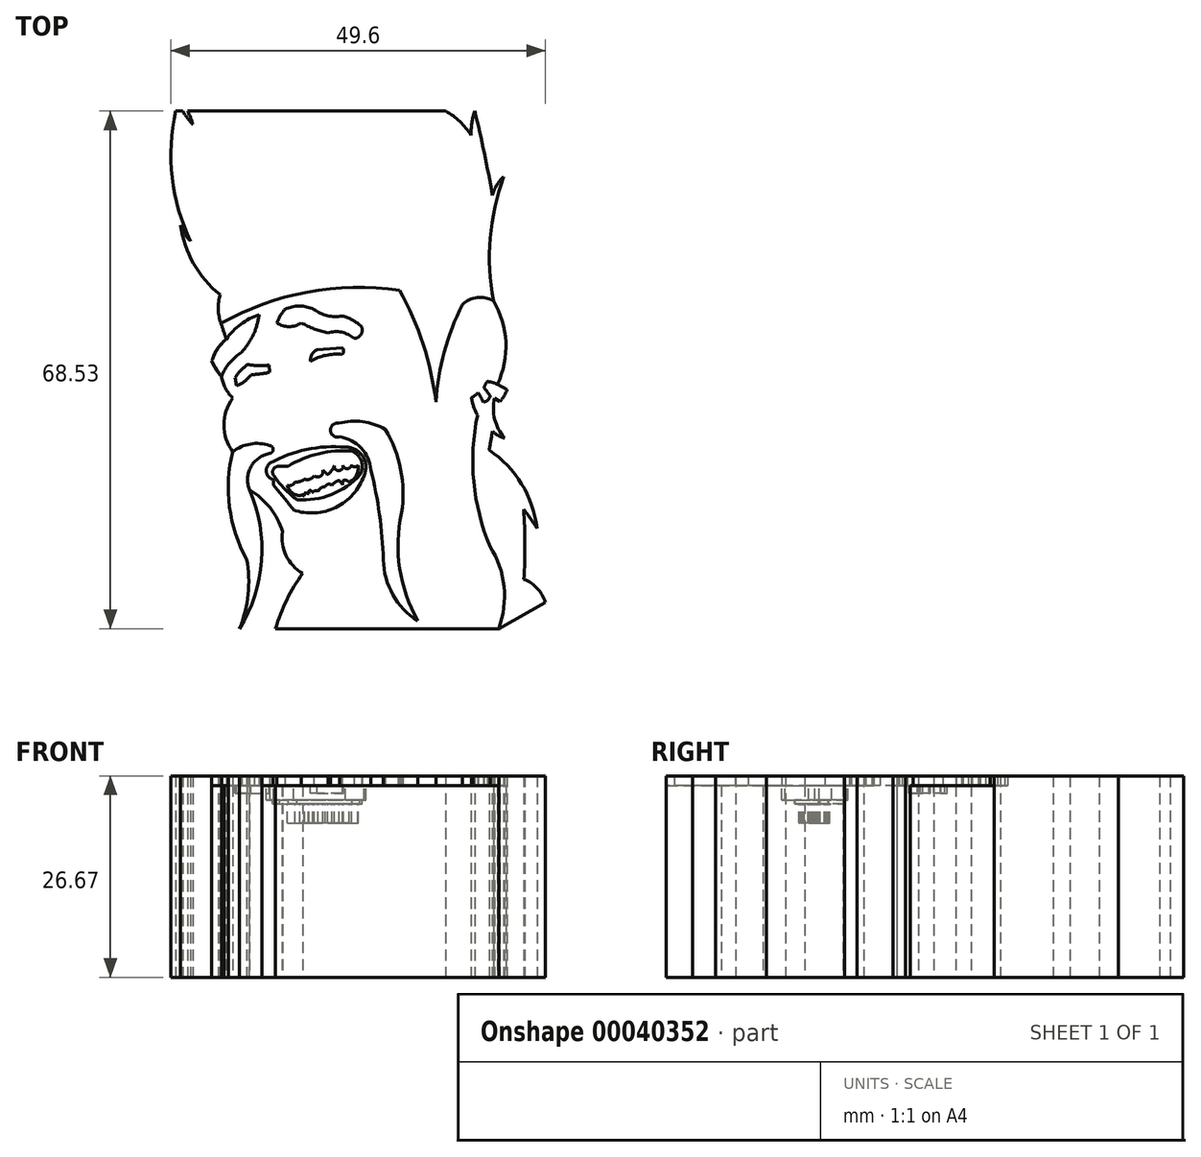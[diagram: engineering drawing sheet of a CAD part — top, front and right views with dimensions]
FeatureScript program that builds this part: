
annotation { "Feature Type Name" : "Feature", "Feature Type Description" : "" }
export const myFeature = defineFeature(function(context is Context, id is Id, definition is map)
    precondition{}
    {
        {
            var Q0;
            Q0=qCreatedBy(makeId("Top.planeOp"),FACE);
            var sketch = newSketch(context, id + "F0", { "sketchPlane" : qUnion([Q0])});
            skPoint(sketch, "E0", {"position": v(10.3, 53.46) * mm});
            skPoint(sketch, "E1", {"position": v(49.25, 68.53) * mm});
            skPoint(sketch, "E2", {"position": v(53.1, 59.84) * mm});
            skPoint(sketch, "E3", {"position": v(51.73, 43.41) * mm});
            skPoint(sketch, "E4", {"position": v(15.54, 44.24) * mm});
            skPoint(sketch, "E5", {"position": v(51.6, 57.35) * mm});
            skPoint(sketch, "E6", {"position": v(52.26, 32.34) * mm});
            skPoint(sketch, "E7", {"position": v(51.24, 31) * mm});
            skPoint(sketch, "E8", {"position": v(50.35, 29.98) * mm});
            skPoint(sketch, "E9", {"position": v(49.07, 29.21) * mm});
            skPoint(sketch, "E10", {"position": v(47.66, 29.02) * mm});
            skPoint(sketch, "E11", {"position": v(49.7, 28.13) * mm});
            skPoint(sketch, "E12", {"position": v(50.86, 28.7) * mm});
            skPoint(sketch, "E13", {"position": v(52.58, 30.04) * mm});
            skPoint(sketch, "E14", {"position": v(53.57, 31.65) * mm});
            skArc(sketch, "E15", {"start": v(52.26, 32.34) * mm, "mid": v(53.39, 37.94) * mm, "end": v(51.73, 43.41) * mm});
            skArc(sketch, "E16", {"start": v(52.58, 30.04) * mm, "mid": v(53.15, 30.8) * mm, "end": v(53.57, 31.65) * mm});
            skLineSegment(sketch, "E17", {"start": v(51.24, 31) * mm, "end": v(52.58, 30.04) * mm});
            skLineSegment(sketch, "E18", {"start": v(53.57, 31.65) * mm, "end": v(52.26, 32.34) * mm});
            skPoint(sketch, "E19", {"position": v(45.4, 68.53) * mm});
            skPoint(sketch, "E20", {"position": v(11.23, 68.53) * mm});
            skPoint(sketch, "E21", {"position": v(10.6, 68.53) * mm});
            skPoint(sketch, "E22", {"position": v(9.67, 68.53) * mm});
            skPoint(sketch, "E23", {"position": v(48.8, 65.33) * mm});
            skPoint(sketch, "E24", {"position": v(11.66, 51.27) * mm});
            skPoint(sketch, "E25", {"position": v(11.94, 66.75) * mm});
            skArc(sketch, "E26", {"start": v(10.6, 68.53) * mm, "mid": v(11.22, 67.6) * mm, "end": v(11.94, 66.75) * mm});
            skArc(sketch, "E27", {"start": v(11.94, 66.75) * mm, "mid": v(11.64, 67.66) * mm, "end": v(11.23, 68.53) * mm});
            skArc(sketch, "E28", {"start": v(48.8, 65.33) * mm, "mid": v(47.3, 67.15) * mm, "end": v(45.4, 68.53) * mm});
            skArc(sketch, "E29", {"start": v(49.25, 68.53) * mm, "mid": v(48.88, 66.95) * mm, "end": v(48.8, 65.33) * mm});
            skArc(sketch, "E30", {"start": v(51.6, 57.35) * mm, "mid": v(50.54, 62.97) * mm, "end": v(49.25, 68.53) * mm});
            skArc(sketch, "E31", {"start": v(53.1, 59.84) * mm, "mid": v(52.17, 58.7) * mm, "end": v(51.6, 57.35) * mm});
            skArc(sketch, "E32", {"start": v(53.1, 59.84) * mm, "mid": v(51.32, 51.72) * mm, "end": v(51.73, 43.41) * mm});
            skArc(sketch, "E33", {"start": v(9.67, 68.53) * mm, "mid": v(9.2, 59.73) * mm, "end": v(11.66, 51.27) * mm});
            skArc(sketch, "E34", {"start": v(10.3, 53.46) * mm, "mid": v(10.85, 52.28) * mm, "end": v(11.66, 51.27) * mm});
            skArc(sketch, "E35", {"start": v(10.3, 53.46) * mm, "mid": v(12.03, 48.34) * mm, "end": v(15.54, 44.24) * mm});
            skLineSegment(sketch, "E36", {"start": v(9.67, 68.53) * mm, "end": v(10.6, 68.53) * mm});
            skLineSegment(sketch, "E37", {"start": v(45.4, 68.53) * mm, "end": v(11.23, 68.53) * mm});
            skPoint(sketch, "E38", {"position": v(15.66, 40.4) * mm});
            skPoint(sketch, "E39", {"position": v(16.37, 38.34) * mm});
            skPoint(sketch, "E40", {"position": v(14.46, 35.44) * mm});
            skPoint(sketch, "E41", {"position": v(15.73, 33.39) * mm});
            skArc(sketch, "E42", {"start": v(15.54, 44.24) * mm, "mid": v(15.3, 42.3) * mm, "end": v(15.66, 40.4) * mm});
            skArc(sketch, "E43", {"start": v(16.37, 38.34) * mm, "mid": v(16.02, 39.37) * mm, "end": v(15.66, 40.4) * mm});
            skArc(sketch, "E44", {"start": v(16.37, 38.34) * mm, "mid": v(15.19, 37.04) * mm, "end": v(14.46, 35.44) * mm});
            skArc(sketch, "E45", {"start": v(14.46, 35.44) * mm, "mid": v(15, 34.35) * mm, "end": v(15.73, 33.39) * mm});
            skPoint(sketch, "E46", {"position": v(48.02, 25.2) * mm});
            skPoint(sketch, "E47", {"position": v(17.2, 30.53) * mm});
            skArc(sketch, "E48", {"start": v(15.73, 33.39) * mm, "mid": v(16.25, 31.84) * mm, "end": v(17.2, 30.53) * mm});
            skArc(sketch, "E49", {"start": v(17.2, 30.53) * mm, "mid": v(16.05, 26.97) * mm, "end": v(17.2, 23.4) * mm});
            skPoint(sketch, "E50", {"position": v(51.9, 30.52) * mm});
            skPoint(sketch, "E51", {"position": v(53.2, 25.24) * mm});
            skPoint(sketch, "E52", {"position": v(51.61, 26.15) * mm});
            skPoint(sketch, "E53", {"position": v(51.17, 23.63) * mm});
            skPoint(sketch, "E54", {"position": v(57.51, 13.28) * mm});
            skPoint(sketch, "E55", {"position": v(55.74, 15.8) * mm});
            skArc(sketch, "E56", {"start": v(51.9, 30.52) * mm, "mid": v(51.9, 27.72) * mm, "end": v(53.2, 25.24) * mm});
            skArc(sketch, "E57", {"start": v(51.61, 26.15) * mm, "mid": v(52.34, 25.59) * mm, "end": v(53.2, 25.24) * mm});
            skArc(sketch, "E58", {"start": v(51.17, 23.63) * mm, "mid": v(51.4, 24.89) * mm, "end": v(51.61, 26.15) * mm});
            skArc(sketch, "E59", {"start": v(57.51, 13.28) * mm, "mid": v(55.47, 19.15) * mm, "end": v(51.17, 23.63) * mm});
            skArc(sketch, "E60", {"start": v(57.51, 13.28) * mm, "mid": v(56.66, 14.56) * mm, "end": v(55.74, 15.8) * mm});
            skPoint(sketch, "E61", {"position": v(55.8, 6.52) * mm});
            skPoint(sketch, "E62", {"position": v(58.63, 3.47) * mm});
            skPoint(sketch, "E63", {"position": v(52.44, 0) * mm});
            skPoint(sketch, "E64", {"position": v(18.11, 0) * mm});
            skPoint(sketch, "E65", {"position": v(22.88, 0) * mm});
            skArc(sketch, "E66", {"start": v(55.8, 6.52) * mm, "mid": v(55.9, 11.16) * mm, "end": v(55.74, 15.8) * mm});
            skArc(sketch, "E67", {"start": v(58.63, 3.47) * mm, "mid": v(57.56, 5.32) * mm, "end": v(55.8, 6.52) * mm});
            skLineSegment(sketch, "E68", {"start": v(58.63, 3.47) * mm, "end": v(52.44, 0) * mm});
            skLineSegment(sketch, "E69", {"start": v(22.88, 0) * mm, "end": v(52.44, 0) * mm});
            skPoint(sketch, "E70", {"position": v(26.46, 7.3) * mm});
            skPoint(sketch, "E71", {"position": v(23.83, 12.83) * mm});
            skPoint(sketch, "E72", {"position": v(19.43, 18.36) * mm});
            skArc(sketch, "E73", {"start": v(18.11, 0) * mm, "mid": v(21.05, 9.01) * mm, "end": v(19.43, 18.36) * mm});
            skArc(sketch, "E74", {"start": v(23.83, 12.83) * mm, "mid": v(22.15, 16) * mm, "end": v(19.43, 18.36) * mm});
            skArc(sketch, "E75", {"start": v(23.83, 12.83) * mm, "mid": v(24.3, 9.66) * mm, "end": v(26.46, 7.3) * mm});
            skArc(sketch, "E76", {"start": v(26.46, 7.3) * mm, "mid": v(24.37, 3.8) * mm, "end": v(22.88, 0) * mm});
            skArc(sketch, "E77", {"start": v(17.2, 23.4) * mm, "mid": v(16.8, 16.12) * mm, "end": v(19.05, 9.19) * mm});
            skArc(sketch, "E78", {"start": v(18.11, 0) * mm, "mid": v(19.26, 4.52) * mm, "end": v(19.05, 9.19) * mm});
            skSolve(sketch);
        }
        {
            var Q0;
            Q0 = qSketchRegion(id + "F0", true);
            extrude(context, id + "F1", {"entities" : qUnion([Q0]), "depth" : 25.4 * mm});
        }
        {
            var Q0;
            Q0=makeQuery(id+"F1.opExtrude","CAP_FACE",FACE,{"disambiguationData":[OSD([sQuery(id+"F0.wireOp",EDGE,"E15"),sQuery(id+"F0.wireOp",EDGE,"E16"),sQuery(id+"F0.wireOp",EDGE,"E17"),sQuery(id+"F0.wireOp",EDGE,"E18"),sQuery(id+"F0.wireOp",EDGE,"E26"),sQuery(id+"F0.wireOp",EDGE,"E27"),sQuery(id+"F0.wireOp",EDGE,"E28"),sQuery(id+"F0.wireOp",EDGE,"E29"),sQuery(id+"F0.wireOp",EDGE,"E30"),sQuery(id+"F0.wireOp",EDGE,"E31"),sQuery(id+"F0.wireOp",EDGE,"E32"),sQuery(id+"F0.wireOp",EDGE,"E33"),sQuery(id+"F0.wireOp",EDGE,"E34"),sQuery(id+"F0.wireOp",EDGE,"E35"),sQuery(id+"F0.wireOp",EDGE,"E36"),sQuery(id+"F0.wireOp",EDGE,"E37"),sQuery(id+"F0.wireOp",EDGE,"E42"),sQuery(id+"F0.wireOp",EDGE,"E43"),sQuery(id+"F0.wireOp",EDGE,"E44"),sQuery(id+"F0.wireOp",EDGE,"E45"),sQuery(id+"F0.wireOp",EDGE,"E48"),sQuery(id+"F0.wireOp",EDGE,"E49"),sQuery(id+"F0.wireOp",EDGE,"E56"),sQuery(id+"F0.wireOp",EDGE,"E57"),sQuery(id+"F0.wireOp",EDGE,"E58"),sQuery(id+"F0.wireOp",EDGE,"E59"),sQuery(id+"F0.wireOp",EDGE,"E60"),sQuery(id+"F0.wireOp",EDGE,"E66"),sQuery(id+"F0.wireOp",EDGE,"E67"),sQuery(id+"F0.wireOp",EDGE,"E68"),sQuery(id+"F0.wireOp",EDGE,"E69"),sQuery(id+"F0.wireOp",EDGE,"E73"),sQuery(id+"F0.wireOp",EDGE,"E74"),sQuery(id+"F0.wireOp",EDGE,"E75"),sQuery(id+"F0.wireOp",EDGE,"E76"),sQuery(id+"F0.wireOp",EDGE,"E77"),sQuery(id+"F0.wireOp",EDGE,"E78")])],"isStart":false});
            var sketch = newSketch(context, id + "F2", { "sketchPlane" : qUnion([Q0])});
            skArc(sketch, "E79", {"start": v(39.3, 44.83) * mm, "mid": v(27.11, 44.57) * mm, "end": v(15.66, 40.4) * mm});
            skArc(sketch, "E80", {"start": v(44.11, 30.03) * mm, "mid": v(42.44, 37.67) * mm, "end": v(39.3, 44.83) * mm});
            skArc(sketch, "E81", {"start": v(47.62, 42.9) * mm, "mid": v(45.24, 36.64) * mm, "end": v(44.11, 30.03) * mm});
            skArc(sketch, "E82", {"start": v(51.73, 43.41) * mm, "mid": v(49.59, 43.85) * mm, "end": v(47.62, 42.9) * mm});
            skArc(sketch, "E83", {"start": v(52.26, 32.34) * mm, "mid": v(53.4, 37.94) * mm, "end": v(51.73, 43.41) * mm});
            skArc(sketch, "E84", {"start": v(16.37, 38.34) * mm, "mid": v(16.1, 39.4) * mm, "end": v(15.66, 40.4) * mm});
            skArc(sketch, "E85", {"start": v(15.73, 33.39) * mm, "mid": v(16.11, 31.77) * mm, "end": v(17.2, 30.53) * mm});
            skArc(sketch, "E86", {"start": v(17.2, 30.53) * mm, "mid": v(16.1, 26.97) * mm, "end": v(17.2, 23.4) * mm});
            skArc(sketch, "E87", {"start": v(22.13, 24.25) * mm, "mid": v(19.57, 24.44) * mm, "end": v(17.2, 23.4) * mm});
            skArc(sketch, "E88", {"start": v(22.13, 23.2) * mm, "mid": v(22.57, 23.73) * mm, "end": v(22.13, 24.25) * mm});
            skArc(sketch, "E89", {"start": v(22.13, 23.2) * mm, "mid": v(19.63, 21.42) * mm, "end": v(19.43, 18.36) * mm});
            skArc(sketch, "E90", {"start": v(23.83, 12.83) * mm, "mid": v(22.08, 15.96) * mm, "end": v(19.43, 18.36) * mm});
            skArc(sketch, "E91", {"start": v(23.83, 12.83) * mm, "mid": v(24.12, 9.58) * mm, "end": v(26.46, 7.3) * mm});
            skArc(sketch, "E92", {"start": v(52.44, 0) * mm, "mid": v(53.15, 5.56) * mm, "end": v(51.3, 10.85) * mm});
            skArc(sketch, "E93", {"start": v(49.63, 28.28) * mm, "mid": v(49.14, 19.44) * mm, "end": v(51.3, 10.85) * mm});
            skArc(sketch, "E94", {"start": v(26.46, 7.3) * mm, "mid": v(27.3, 4.4) * mm, "end": v(29.14, 2) * mm});
            skArc(sketch, "E95", {"start": v(29.14, 2) * mm, "mid": v(40.75, 0.5) * mm, "end": v(52.44, 0) * mm});
            skArc(sketch, "E96", {"start": v(52.26, 32.34) * mm, "mid": v(51.62, 32.6) * mm, "end": v(50.94, 32.71) * mm});
            skArc(sketch, "E97", {"start": v(50.94, 32.71) * mm, "mid": v(50.67, 32.33) * mm, "end": v(50.48, 31.91) * mm});
            skArc(sketch, "E98", {"start": v(51.31, 30.82) * mm, "mid": v(50.9, 31.38) * mm, "end": v(50.48, 31.91) * mm});
            skArc(sketch, "E99", {"start": v(50.4, 29.97) * mm, "mid": v(50.99, 30.26) * mm, "end": v(51.31, 30.82) * mm});
            skArc(sketch, "E100", {"start": v(50.4, 29.97) * mm, "mid": v(50.1, 30.61) * mm, "end": v(49.71, 31.22) * mm});
            skArc(sketch, "E101", {"start": v(48.83, 30.6) * mm, "mid": v(49.3, 30.87) * mm, "end": v(49.71, 31.22) * mm});
            skArc(sketch, "E102", {"start": v(48.83, 30.6) * mm, "mid": v(49.12, 29.4) * mm, "end": v(49.63, 28.28) * mm});
            skArc(sketch, "E103", {"start": v(31.28, 27.2) * mm, "mid": v(30.17, 26.23) * mm, "end": v(31.39, 25.4) * mm});
            skArc(sketch, "E104", {"start": v(37.42, 26.41) * mm, "mid": v(34.43, 27.4) * mm, "end": v(31.28, 27.2) * mm});
            skArc(sketch, "E105", {"start": v(35.52, 21) * mm, "mid": v(34.21, 23.92) * mm, "end": v(31.39, 25.4) * mm});
            skArc(sketch, "E106", {"start": v(39.57, 15.3) * mm, "mid": v(39.46, 21.04) * mm, "end": v(37.42, 26.41) * mm});
            skArc(sketch, "E107", {"start": v(39.57, 15.3) * mm, "mid": v(39.32, 7.97) * mm, "end": v(41.72, 1.04) * mm});
            skArc(sketch, "E108", {"start": v(37.17, 9.1) * mm, "mid": v(38.43, 4.5) * mm, "end": v(41.72, 1.04) * mm});
            skArc(sketch, "E109", {"start": v(37.17, 9.1) * mm, "mid": v(36.66, 15.1) * mm, "end": v(35.52, 21) * mm});
            skArc(sketch, "E110", {"start": v(24.1, 42.28) * mm, "mid": v(23.53, 41.42) * mm, "end": v(23.08, 40.48) * mm});
            skArc(sketch, "E111", {"start": v(27.97, 42.28) * mm, "mid": v(26.04, 42.7) * mm, "end": v(24.1, 42.28) * mm});
            skArc(sketch, "E112", {"start": v(27.97, 42.28) * mm, "mid": v(29.75, 41.45) * mm, "end": v(31.7, 41.38) * mm});
            skArc(sketch, "E113", {"start": v(34.28, 39.97) * mm, "mid": v(33.1, 40.86) * mm, "end": v(31.7, 41.38) * mm});
            skArc(sketch, "E114", {"start": v(33.25, 38.42) * mm, "mid": v(34.17, 38.92) * mm, "end": v(34.28, 39.97) * mm});
            skArc(sketch, "E115", {"start": v(33.25, 38.42) * mm, "mid": v(31.64, 39.26) * mm, "end": v(29.84, 39.13) * mm});
            skArc(sketch, "E116", {"start": v(23.08, 40.48) * mm, "mid": v(24.69, 40) * mm, "end": v(26.3, 40.48) * mm});
            skArc(sketch, "E117", {"start": v(26.3, 40.48) * mm, "mid": v(28.02, 39.68) * mm, "end": v(29.84, 39.13) * mm});
            skPoint(sketch, "E118", {"position": v(20.7, 41.58) * mm});
            skPoint(sketch, "E119", {"position": v(18.45, 36.62) * mm});
            skArc(sketch, "E120", {"start": v(20.7, 41.58) * mm, "mid": v(18.28, 40.3) * mm, "end": v(16.37, 38.34) * mm});
            skArc(sketch, "E121", {"start": v(18.45, 36.62) * mm, "mid": v(16.83, 35.22) * mm, "end": v(15.73, 33.39) * mm});
            skArc(sketch, "E122", {"start": v(16.37, 38.34) * mm, "mid": v(15.21, 37.02) * mm, "end": v(14.46, 35.44) * mm});
            skArc(sketch, "E123", {"start": v(14.46, 35.44) * mm, "mid": v(15.05, 34.39) * mm, "end": v(15.73, 33.39) * mm});
            skArc(sketch, "E124", {"start": v(20.06, 39.13) * mm, "mid": v(20.46, 40.33) * mm, "end": v(20.7, 41.58) * mm});
            skArc(sketch, "E125", {"start": v(18.45, 36.62) * mm, "mid": v(19.32, 37.83) * mm, "end": v(20.06, 39.13) * mm});
            skSolve(sketch);
        }
        {
            var Q0;
            Q0=makeQuery(id+"F2.imprint","IMPRINT",FACE,{"disambiguationData":[TD([[makeQuery(id+"F2.imprint","IMPRINT",EDGE,{"derivedFrom":sQuery(id+"F2.wireOp",EDGE,"E79")}),-1.0]])]});
            var Q1;
            Q1=makeQuery(id+"F2.imprint","IMPRINT",FACE,{"disambiguationData":[TD([[makeQuery(id+"F2.imprint","IMPRINT",EDGE,{"derivedFrom":sQuery(id+"F2.wireOp",EDGE,"E92")}),-1.0]])]});
            var Q2;
            Q2=makeQuery(id+"F2.imprint","IMPRINT",FACE,{"disambiguationData":[TD([[makeQuery(id+"F2.imprint","IMPRINT",EDGE,{"derivedFrom":sQuery(id+"F2.wireOp",EDGE,"E87")}),1.0]])]});
            var Q3;
            Q3=makeQuery(id+"F2.imprint","IMPRINT",FACE,{"disambiguationData":[TD([[makeQuery(id+"F2.imprint","IMPRINT",EDGE,{"derivedFrom":sQuery(id+"F2.wireOp",EDGE,"E103")}),1.0]])]});
            var Q4;
            Q4=makeQuery(id+"F2.imprint","IMPRINT",FACE,{"disambiguationData":[TD([[makeQuery(id+"F2.imprint","IMPRINT",EDGE,{"derivedFrom":sQuery(id+"F2.wireOp",EDGE,"E110")}),1.0]])]});
            var Q5;
            Q5=makeQuery(id+"F2.imprint","IMPRINT",FACE,{"disambiguationData":[TD([[makeQuery(id+"F2.imprint","IMPRINT",EDGE,{"derivedFrom":sQuery(id+"F2.wireOp",EDGE,"E120")}),1.0]])]});
            extrude(context, id + "F3", {"entities" : qUnion([Q0, Q1, Q2, Q3, Q4, Q5]), "operationType" : NewBodyOperationType.ADD, "depth" : 1.27 * mm});
        }
        {
            var Q0;
            Q0=makeQuery(id+"F1.opExtrude","CAP_FACE",FACE,{"disambiguationData":[OSD([sQuery(id+"F0.wireOp",EDGE,"E15"),sQuery(id+"F0.wireOp",EDGE,"E16"),sQuery(id+"F0.wireOp",EDGE,"E17"),sQuery(id+"F0.wireOp",EDGE,"E18"),sQuery(id+"F0.wireOp",EDGE,"E26"),sQuery(id+"F0.wireOp",EDGE,"E27"),sQuery(id+"F0.wireOp",EDGE,"E28"),sQuery(id+"F0.wireOp",EDGE,"E29"),sQuery(id+"F0.wireOp",EDGE,"E30"),sQuery(id+"F0.wireOp",EDGE,"E31"),sQuery(id+"F0.wireOp",EDGE,"E32"),sQuery(id+"F0.wireOp",EDGE,"E33"),sQuery(id+"F0.wireOp",EDGE,"E34"),sQuery(id+"F0.wireOp",EDGE,"E35"),sQuery(id+"F0.wireOp",EDGE,"E36"),sQuery(id+"F0.wireOp",EDGE,"E37"),sQuery(id+"F0.wireOp",EDGE,"E42"),sQuery(id+"F0.wireOp",EDGE,"E43"),sQuery(id+"F0.wireOp",EDGE,"E44"),sQuery(id+"F0.wireOp",EDGE,"E45"),sQuery(id+"F0.wireOp",EDGE,"E48"),sQuery(id+"F0.wireOp",EDGE,"E49"),sQuery(id+"F0.wireOp",EDGE,"E56"),sQuery(id+"F0.wireOp",EDGE,"E57"),sQuery(id+"F0.wireOp",EDGE,"E58"),sQuery(id+"F0.wireOp",EDGE,"E59"),sQuery(id+"F0.wireOp",EDGE,"E60"),sQuery(id+"F0.wireOp",EDGE,"E66"),sQuery(id+"F0.wireOp",EDGE,"E67"),sQuery(id+"F0.wireOp",EDGE,"E68"),sQuery(id+"F0.wireOp",EDGE,"E69"),sQuery(id+"F0.wireOp",EDGE,"E73"),sQuery(id+"F0.wireOp",EDGE,"E74"),sQuery(id+"F0.wireOp",EDGE,"E75"),sQuery(id+"F0.wireOp",EDGE,"E76"),sQuery(id+"F0.wireOp",EDGE,"E77"),sQuery(id+"F0.wireOp",EDGE,"E78")])],"isStart":false});
            var sketch = newSketch(context, id + "F4", { "sketchPlane" : qUnion([Q0])});
            skArc(sketch, "E126", {"start": v(31.74, 36.32) * mm, "mid": v(29.56, 36.2) * mm, "end": v(27.53, 35.41) * mm});
            skArc(sketch, "E127", {"start": v(28.36, 36.9) * mm, "mid": v(27.71, 36.3) * mm, "end": v(27.53, 35.41) * mm});
            skArc(sketch, "E128", {"start": v(31.74, 36.32) * mm, "mid": v(31.91, 36.75) * mm, "end": v(31.74, 37.19) * mm});
            skLineSegment(sketch, "E129", {"start": v(28.36, 36.9) * mm, "end": v(31.74, 37.19) * mm});
            skPoint(sketch, "E130", {"position": v(19.66, 33.64) * mm});
            skPoint(sketch, "E131", {"position": v(19.2, 34.96) * mm});
            skPoint(sketch, "E132", {"position": v(22.06, 34.89) * mm});
            skPoint(sketch, "E133", {"position": v(22.1, 33.95) * mm});
            skPoint(sketch, "E134", {"position": v(17.74, 32.14) * mm});
            skPoint(sketch, "E135", {"position": v(17.57, 33.25) * mm});
            skArc(sketch, "E136", {"start": v(17.74, 32.14) * mm, "mid": v(18.8, 32.75) * mm, "end": v(19.66, 33.64) * mm});
            skArc(sketch, "E137", {"start": v(19.2, 34.96) * mm, "mid": v(18.3, 34.2) * mm, "end": v(17.57, 33.25) * mm});
            skArc(sketch, "E138", {"start": v(19.2, 34.96) * mm, "mid": v(20.63, 34.82) * mm, "end": v(22.06, 34.89) * mm});
            skArc(sketch, "E139", {"start": v(19.66, 33.64) * mm, "mid": v(20.88, 33.72) * mm, "end": v(22.1, 33.95) * mm});
            skLineSegment(sketch, "E140", {"start": v(17.57, 33.25) * mm, "end": v(17.74, 32.14) * mm});
            skLineSegment(sketch, "E141", {"start": v(22.06, 34.89) * mm, "end": v(22.1, 33.95) * mm});
            skSolve(sketch);
        }
        {
            var Q0;
            Q0 = qSketchRegion(id + "F4", true);
            extrude(context, id + "F5", {"entities" : qUnion([Q0]), "operationType" : NewBodyOperationType.REMOVE, "oppositeDirection" : true, "depth" : 1.02 * mm});
        }
        {
            var Q0;
            Q0=makeQuery(id+"F1.opExtrude","CAP_FACE",FACE,{"disambiguationData":[OSD([sQuery(id+"F0.wireOp",EDGE,"E15"),sQuery(id+"F0.wireOp",EDGE,"E16"),sQuery(id+"F0.wireOp",EDGE,"E17"),sQuery(id+"F0.wireOp",EDGE,"E18"),sQuery(id+"F0.wireOp",EDGE,"E26"),sQuery(id+"F0.wireOp",EDGE,"E27"),sQuery(id+"F0.wireOp",EDGE,"E28"),sQuery(id+"F0.wireOp",EDGE,"E29"),sQuery(id+"F0.wireOp",EDGE,"E30"),sQuery(id+"F0.wireOp",EDGE,"E31"),sQuery(id+"F0.wireOp",EDGE,"E32"),sQuery(id+"F0.wireOp",EDGE,"E33"),sQuery(id+"F0.wireOp",EDGE,"E34"),sQuery(id+"F0.wireOp",EDGE,"E35"),sQuery(id+"F0.wireOp",EDGE,"E36"),sQuery(id+"F0.wireOp",EDGE,"E37"),sQuery(id+"F0.wireOp",EDGE,"E42"),sQuery(id+"F0.wireOp",EDGE,"E43"),sQuery(id+"F0.wireOp",EDGE,"E44"),sQuery(id+"F0.wireOp",EDGE,"E45"),sQuery(id+"F0.wireOp",EDGE,"E48"),sQuery(id+"F0.wireOp",EDGE,"E49"),sQuery(id+"F0.wireOp",EDGE,"E56"),sQuery(id+"F0.wireOp",EDGE,"E57"),sQuery(id+"F0.wireOp",EDGE,"E58"),sQuery(id+"F0.wireOp",EDGE,"E59"),sQuery(id+"F0.wireOp",EDGE,"E60"),sQuery(id+"F0.wireOp",EDGE,"E66"),sQuery(id+"F0.wireOp",EDGE,"E67"),sQuery(id+"F0.wireOp",EDGE,"E68"),sQuery(id+"F0.wireOp",EDGE,"E69"),sQuery(id+"F0.wireOp",EDGE,"E73"),sQuery(id+"F0.wireOp",EDGE,"E74"),sQuery(id+"F0.wireOp",EDGE,"E75"),sQuery(id+"F0.wireOp",EDGE,"E76"),sQuery(id+"F0.wireOp",EDGE,"E77"),sQuery(id+"F0.wireOp",EDGE,"E78")])],"isStart":false});
            var sketch = newSketch(context, id + "F6", { "sketchPlane" : qUnion([Q0])});
            skPoint(sketch, "E142", {"position": v(22.75, 19.68) * mm});
            skPoint(sketch, "E143", {"position": v(22.2, 21.91) * mm});
            skArc(sketch, "E144", {"start": v(22.2, 21.91) * mm, "mid": v(21.7, 20.6) * mm, "end": v(22.75, 19.68) * mm});
            skArc(sketch, "E145", {"start": v(32.16, 24.01) * mm, "mid": v(27.02, 23.71) * mm, "end": v(22.2, 21.91) * mm});
            skArc(sketch, "E146", {"start": v(34.59, 20.26) * mm, "mid": v(34.44, 22.83) * mm, "end": v(32.16, 24.01) * mm});
            skArc(sketch, "E147", {"start": v(22.75, 19.68) * mm, "mid": v(22.58, 19.27) * mm, "end": v(22.75, 18.86) * mm});
            skArc(sketch, "E148", {"start": v(25.27, 15.7) * mm, "mid": v(24.04, 17.3) * mm, "end": v(22.75, 18.86) * mm});
            skArc(sketch, "E149", {"start": v(25.27, 15.7) * mm, "mid": v(30.88, 16.05) * mm, "end": v(34.59, 20.26) * mm});
            skSolve(sketch);
        }
        {
            var Q0;
            Q0 = qSketchRegion(id + "F6", true);
            extrude(context, id + "F7", {"entities" : qUnion([Q0]), "operationType" : NewBodyOperationType.REMOVE, "oppositeDirection" : true, "depth" : 1.9 * mm});
        }
        {
            var Q0;
            Q0=makeQuery(id+"F7.boolean.opBoolean","COPY",FACE,{"derivedFrom":makeQuery(id+"F7.opExtrude","CAP_FACE",FACE,{"disambiguationData":[OSD([sQuery(id+"F6.wireOp",EDGE,"E144"),sQuery(id+"F6.wireOp",EDGE,"E145"),sQuery(id+"F6.wireOp",EDGE,"E146"),sQuery(id+"F6.wireOp",EDGE,"E147"),sQuery(id+"F6.wireOp",EDGE,"E148"),sQuery(id+"F6.wireOp",EDGE,"E149")])],"isStart":false})});
            var sketch = newSketch(context, id + "F8", { "sketchPlane" : qUnion([Q0])});
            skArc(sketch, "E150", {"start": v(23.42, 21.49) * mm, "mid": v(22.6, 21.08) * mm, "end": v(22.72, 20.17) * mm});
            skArc(sketch, "E151", {"start": v(33.02, 23.5) * mm, "mid": v(28.64, 23.17) * mm, "end": v(24.57, 21.5) * mm});
            skArc(sketch, "E152", {"start": v(23.42, 21.49) * mm, "mid": v(24, 21.48) * mm, "end": v(24.57, 21.5) * mm});
            skArc(sketch, "E153", {"start": v(22.72, 20.17) * mm, "mid": v(24.1, 18.5) * mm, "end": v(25.74, 17.06) * mm});
            skArc(sketch, "E154", {"start": v(25.74, 17.06) * mm, "mid": v(30.28, 17.75) * mm, "end": v(34.06, 20.34) * mm});
            skArc(sketch, "E155", {"start": v(34.06, 20.34) * mm, "mid": v(34.27, 22.16) * mm, "end": v(33.02, 23.5) * mm});
            skSolve(sketch);
        }
        {
            var Q0;
            Q0 = qSketchRegion(id + "F8", true);
            extrude(context, id + "F9", {"entities" : qUnion([Q0]), "operationType" : NewBodyOperationType.REMOVE, "oppositeDirection" : true, "depth" : 0.5 * mm});
        }
        {
            var Q0;
            Q0=makeQuery(id+"F9.boolean.opBoolean","COPY",FACE,{"derivedFrom":makeQuery(id+"F9.opExtrude","CAP_FACE",FACE,{"disambiguationData":[OSD([sQuery(id+"F8.wireOp",EDGE,"E150"),sQuery(id+"F8.wireOp",EDGE,"E151"),sQuery(id+"F8.wireOp",EDGE,"E152"),sQuery(id+"F8.wireOp",EDGE,"E153"),sQuery(id+"F8.wireOp",EDGE,"E154"),sQuery(id+"F8.wireOp",EDGE,"E155")])],"isStart":false})});
            var sketch = newSketch(context, id + "F10", { "sketchPlane" : qUnion([Q0])});
            skPoint(sketch, "E156", {"position": v(25.45, 19.38) * mm});
            skPoint(sketch, "E157", {"position": v(26.73, 19.8) * mm});
            skPoint(sketch, "E158", {"position": v(27.99, 20.24) * mm});
            skPoint(sketch, "E159", {"position": v(29.15, 20.97) * mm});
            skPoint(sketch, "E160", {"position": v(30.65, 21.56) * mm});
            skPoint(sketch, "E161", {"position": v(31.82, 21.66) * mm});
            skPoint(sketch, "E162", {"position": v(32.94, 21.63) * mm});
            skArc(sketch, "E163", {"start": v(24.43, 18.95) * mm, "mid": v(25.02, 18.99) * mm, "end": v(25.45, 19.38) * mm});
            skArc(sketch, "E164", {"start": v(25.45, 19.38) * mm, "mid": v(26.13, 19.49) * mm, "end": v(26.73, 19.8) * mm});
            skArc(sketch, "E165", {"start": v(26.73, 19.8) * mm, "mid": v(27.44, 19.78) * mm, "end": v(27.99, 20.24) * mm});
            skArc(sketch, "E166", {"start": v(27.99, 20.24) * mm, "mid": v(28.84, 20.18) * mm, "end": v(29.15, 20.97) * mm});
            skArc(sketch, "E167", {"start": v(29.76, 20.4) * mm, "mid": v(29.47, 20.7) * mm, "end": v(29.15, 20.97) * mm});
            skArc(sketch, "E168", {"start": v(29.76, 20.4) * mm, "mid": v(30.3, 20.9) * mm, "end": v(30.65, 21.56) * mm});
            skArc(sketch, "E169", {"start": v(30.65, 21.56) * mm, "mid": v(31.3, 20.92) * mm, "end": v(31.82, 21.66) * mm});
            skArc(sketch, "E170", {"start": v(31.82, 21.66) * mm, "mid": v(32.37, 21.17) * mm, "end": v(32.94, 21.63) * mm});
            skArc(sketch, "E171", {"start": v(32.94, 21.63) * mm, "mid": v(33.37, 21.42) * mm, "end": v(33.8, 21.63) * mm});
            skArc(sketch, "E172", {"start": v(32.62, 19.42) * mm, "mid": v(33.6, 20.31) * mm, "end": v(33.8, 21.63) * mm});
            skArc(sketch, "E173", {"start": v(32.62, 19.42) * mm, "mid": v(32.27, 19.62) * mm, "end": v(31.86, 19.65) * mm});
            skArc(sketch, "E174", {"start": v(26.66, 17.55) * mm, "mid": v(26.4, 17.67) * mm, "end": v(26.14, 17.6) * mm});
            skArc(sketch, "E175", {"start": v(26.7, 17.93) * mm, "mid": v(26.67, 17.74) * mm, "end": v(26.66, 17.55) * mm});
            skArc(sketch, "E176", {"start": v(27.72, 18.15) * mm, "mid": v(27.52, 18.29) * mm, "end": v(27.3, 18.21) * mm});
            skArc(sketch, "E177", {"start": v(27.3, 18.21) * mm, "mid": v(27.27, 18.05) * mm, "end": v(27.3, 17.88) * mm});
            skArc(sketch, "E178", {"start": v(27.3, 17.88) * mm, "mid": v(27, 17.92) * mm, "end": v(26.7, 17.93) * mm});
            skArc(sketch, "E179", {"start": v(27.72, 18.15) * mm, "mid": v(27.76, 18.1) * mm, "end": v(27.83, 18.05) * mm});
            skArc(sketch, "E180", {"start": v(28.55, 18.2) * mm, "mid": v(28.16, 18.27) * mm, "end": v(27.83, 18.05) * mm});
            skArc(sketch, "E181", {"start": v(29.47, 18.8) * mm, "mid": v(28.92, 18.63) * mm, "end": v(28.55, 18.2) * mm});
            skArc(sketch, "E182", {"start": v(30.35, 18.98) * mm, "mid": v(29.86, 19.12) * mm, "end": v(29.47, 18.8) * mm});
            skArc(sketch, "E183", {"start": v(31.3, 19.64) * mm, "mid": v(30.77, 19.38) * mm, "end": v(30.35, 18.98) * mm});
            skArc(sketch, "E184", {"start": v(31.77, 19.04) * mm, "mid": v(31.55, 19.35) * mm, "end": v(31.3, 19.64) * mm});
            skArc(sketch, "E185", {"start": v(31.86, 19.65) * mm, "mid": v(31.78, 19.35) * mm, "end": v(31.77, 19.04) * mm});
            skArc(sketch, "E186", {"start": v(24.43, 18.95) * mm, "mid": v(25.07, 18) * mm, "end": v(26.14, 17.6) * mm});
            skSolve(sketch);
        }
        {
            var Q0;
            Q0=makeQuery(id+"F10.imprint","IMPRINT",FACE,{"disambiguationData":[TD([[makeQuery(id+"F10.imprint","IMPRINT",EDGE,{"derivedFrom":sQuery(id+"F10.wireOp",EDGE,"E163")}),-1.0]])]});
            extrude(context, id + "F11", {"entities" : qUnion([Q0]), "operationType" : NewBodyOperationType.REMOVE, "oppositeDirection" : true, "depth" : 2.54 * mm});
        }
    });
